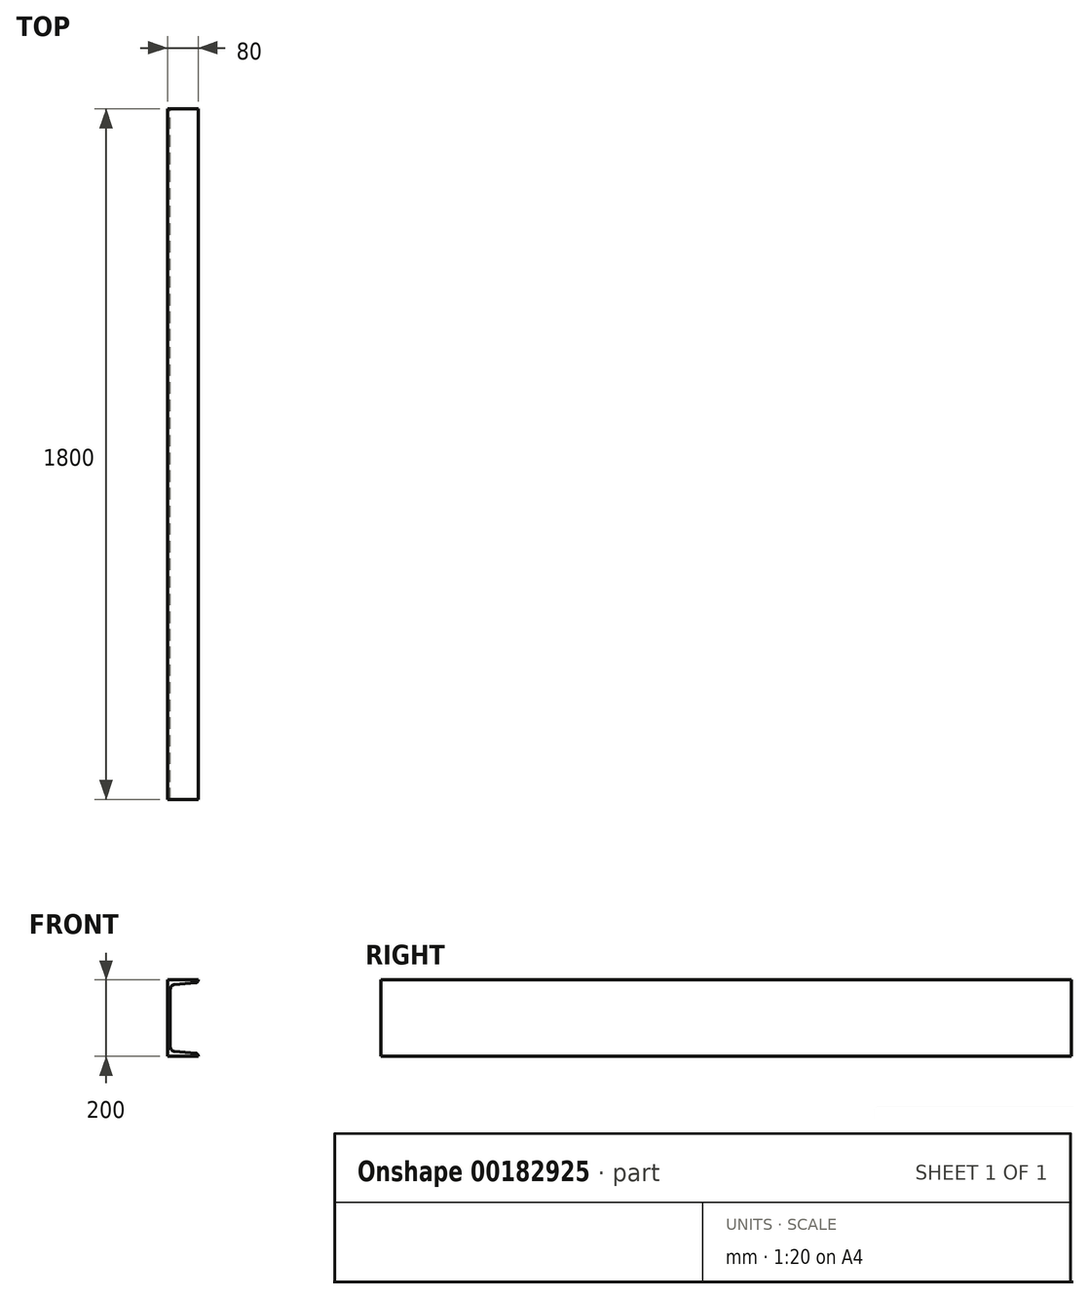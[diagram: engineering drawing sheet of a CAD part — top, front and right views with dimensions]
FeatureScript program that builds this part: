
annotation { "Feature Type Name" : "Feature", "Feature Type Description" : "" }
export const myFeature = defineFeature(function(context is Context, id is Id, definition is map)
    precondition{}
    {
        {
            var Q0;
            Q0=qCreatedBy(makeId("Front.planeOp"),FACE);
            var sketch = newSketch(context, id + "F0", { "sketchPlane" : qUnion([Q0])});
            skLineSegment(sketch, "E0.bottom", {"start": v(0, 0) * mm, "end": v(80, 0) * mm});
            skLineSegment(sketch, "E0.top", {"start": v(0, 100) * mm, "end": v(80, 100) * mm});
            skLineSegment(sketch, "E0.left", {"start": v(0, 0) * mm, "end": v(0, 100) * mm});
            skLineSegment(sketch, "E0.right", {"start": v(80, 98) * mm, "end": v(80, 100) * mm});
            skLineSegment(sketch, "E1.0", {"start": v(7.5, 0) * mm, "end": v(7.5, 75.16) * mm});
            skLineSegment(sketch, "E2", {"start": v(40, 100) * mm, "end": v(40, 89) * mm});
            skLineSegment(sketch, "E3.0", {"start": v(7.5, 89) * mm, "end": v(80, 89) * mm});
            skPoint(sketch, "E4.orphan", {"position": v(40, 0) * mm});
            skLineSegment(sketch, "E5", {"start": v(40, 89) * mm, "end": v(74.52, 92.02) * mm});
            skLineSegment(sketch, "E6", {"start": v(40, 89) * mm, "end": v(18.45, 87.11) * mm});
            skPoint(sketch, "E7.newPointB", {"position": v(80, 0) * mm});
            skArc(sketch, "E7.filletArc", {"start": v(74.52, 92.02) * mm, "mid": v(78.42, 93.94) * mm, "end": v(80, 98) * mm});
            skArc(sketch, "E8.filletArc", {"start": v(18.45, 87.11) * mm, "mid": v(10.65, 83.27) * mm, "end": v(7.5, 75.16) * mm});
            skLineSegment(sketch, "E9.MirrorCS", {"start": v(80, -98) * mm, "end": v(80, -100) * mm});
            skLineSegment(sketch, "E10.MirrorCS", {"start": v(40, -100) * mm, "end": v(40, -89) * mm});
            skArc(sketch, "E11.MirrorCS", {"start": v(74.52, -92.02) * mm, "mid": v(78.42, -93.94) * mm, "end": v(80, -98) * mm});
            skLineSegment(sketch, "E12.MirrorCS", {"start": v(0, -100) * mm, "end": v(80, -100) * mm});
            skLineSegment(sketch, "E13.MirrorCS", {"start": v(7.5, -89) * mm, "end": v(80, -89) * mm});
            skLineSegment(sketch, "E14.MirrorCS", {"start": v(40, -89) * mm, "end": v(74.52, -92.02) * mm});
            skLineSegment(sketch, "E15.MirrorCS", {"start": v(40, -89) * mm, "end": v(18.45, -87.11) * mm});
            skLineSegment(sketch, "E16.MirrorCS", {"start": v(0, 0) * mm, "end": v(0, -100) * mm});
            skArc(sketch, "E17.MirrorCS", {"start": v(18.45, -87.11) * mm, "mid": v(10.65, -83.27) * mm, "end": v(7.5, -75.16) * mm});
            skLineSegment(sketch, "E18.MirrorCS", {"start": v(7.5, 0) * mm, "end": v(7.5, -75.16) * mm});
            skSolve(sketch);
        }
        {
            var Q0;
            {var subQ1=sQuery(id+"F0.wireOp",EDGE,"E0.left");Q0=makeQuery(id+"F0.imprint","IMPRINT",FACE,{"disambiguationData":[TD([[makeQuery(id+"F0.imprint","IMPRINT",EDGE,{"derivedFrom":subQ1}),-1.0]])]});}
            var Q1;
            {var subQ1=sQuery(id+"F0.wireOp",EDGE,"E0.right");Q1=makeQuery(id+"F0.imprint","IMPRINT",FACE,{"disambiguationData":[TD([[makeQuery(id+"F0.imprint","IMPRINT",EDGE,{"derivedFrom":subQ1}),1.0]])]});}
            var Q2;
            {var subQ1=sQuery(id+"F0.wireOp",EDGE,"E10.MirrorCS");Q2=makeQuery(id+"F0.imprint","IMPRINT",FACE,{"disambiguationData":[TD([[makeQuery(id+"F0.imprint","IMPRINT",EDGE,{"derivedFrom":subQ1}),1.0]])]});}
            var Q3;
            {var subQ1=sQuery(id+"F0.wireOp",EDGE,"E9.MirrorCS");Q3=makeQuery(id+"F0.imprint","IMPRINT",FACE,{"disambiguationData":[TD([[makeQuery(id+"F0.imprint","IMPRINT",EDGE,{"derivedFrom":subQ1}),-1.0]])]});}
            extrude(context, id + "F1", {"entities" : qUnion([Q0, Q1, Q2, Q3]), "endBound" : BoundingType.SYMMETRIC, "depth" : 1800 * mm});
        }
    });
